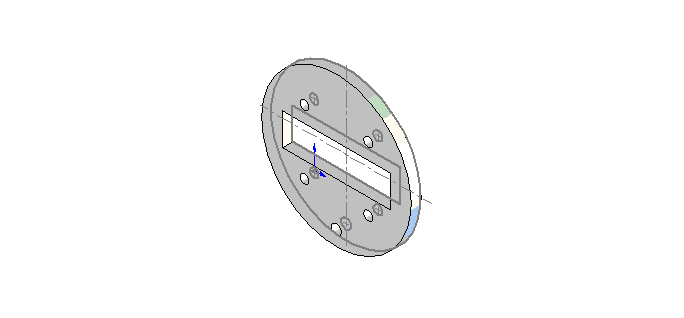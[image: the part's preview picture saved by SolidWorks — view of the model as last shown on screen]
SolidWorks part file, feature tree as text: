
SOLIDWORKS PART (.sldprt)
format: sldprt  version: not decoded by parser v0  size: 153,088 bytes
history: native  units: mm
features: sketch x4, plane x3, extrude x1 + 1 further entry (+7 scaffold rows collapsed)
feature tree (16):
  scaffold x7  (default folders/planes/origin — collapsed)
  "Corps de surface"
  plane  "Face"
  plane  "Dessus"
  plane  "Droite"
  sketch  "Esquisse1"  dims[c1.D1=4.8mm c1.D2=4.8mm c1.D7=4.8mm c1.D8=4.8mm c1.D17=~42.860884mm c1.D18=~42.860884mm c1.D3=32.0mm c1.D4=4.8mm c1.D5=8.0mm c1.D6=8.0mm c2.D7=4.8mm c2.D4=4.0mm c2.D5=5.6mm c2.D6=48.0mm c2.D9=32.0mm c2.D10=4.0mm c2.D11=5.6mm c2.D12=48.0mm c2.D13=28.8mm c2.D14=8.0mm c2.D15=8.0mm c2.D16=16.0mm c2.D18=48.0mm c3.D16=16.0mm c3.D17=8.0mm c3.D18=8.0mm c3.D19=4.0mm c3.D20=4.0mm c3.D21=24.0mm c3.D22=25.0mm c3.D13=28.8mm c3.D3=64.0mm c3.D12=8.0mm c4.D17=8.0mm c4.D9=8.0mm c4.D12=64.0mm c5.D17=48.0mm c5.D18=8.0mm c5.D9=32.0mm c6.D17=16.0mm c6.D18=16.0mm]
  sketch  "Esquisse5"  dims[c1.D12=2.1mm c1.D16=2.1mm c1.D1=8.0mm c1.D2=8.0mm c1.D3=4.0mm c1.D4=4.0mm c1.D5=25.0mm c1.D6=24.0mm c1.D7=12.5mm c1.D8=9.6mm c1.D9=5.5mm c1.D10=20.8mm c1.D11=10.4mm c1.D13=9.5mm c1.D14=2.0mm c1.D15=12.5mm c2.D16=~5.972653mm]
  sketch  "Esquisse7"  dims[c1.D1=75.0mm c1.D2=60.0mm c1.D3=3.1mm c1.D4=33.5mm c1.D5=33.5mm c2.D5=45.0deg c2.D6=~23.688077mm]
  sketch  "Esquisse6"  dims[c1.D1=75.0mm c1.D5=5.0mm c1.D6=5.0mm c1.D7=3.0mm c1.D8=5.0mm c1.D9=2.1mm c1.D10=2.1mm c1.D11=2.1mm c1.D12=2.1mm c1.D13=3.1mm c1.D14=3.1mm c1.D15=3.1mm c1.D16=3.1mm c2.D6=5.0mm c2.D11=4.8mm c2.D7=4.5mm c2.D2=2.5mm c2.D3=2.5mm c2.D4=2.0mm c3.D2=10.0mm c3.D3=3.0mm c3.D4=5.0mm c3.D5=5.0mm c3.D6=~8.062957mm c3.D9=~7.737043mm c3.D10=15.8mm c4.D2=8.0mm c4.D3=8.0mm c4.D6=22.0mm c4.D9=10.0mm c4.D10=16.0mm c4.D11=16.0mm c5.D6=30.0mm]
  extrude  "Extrusion3"  Depth=5mm
decode coverage: 5 of 5 modeling features carry decoded parameters; 1 rows unclassified (native names shown)
note: ~ marks probable driven/reference dimensions
note: suppression state not decoded; provenance and decode notes live in map.json
